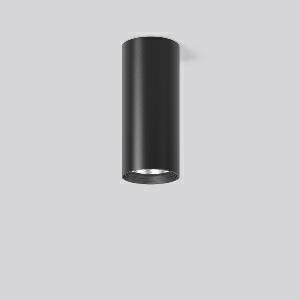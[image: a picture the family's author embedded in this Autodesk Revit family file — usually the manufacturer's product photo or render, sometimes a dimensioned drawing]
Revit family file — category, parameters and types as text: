
# Revit family: heledon_mini_a_931202_003_2_4c84
name_source: partatom
category: Lighting Fixtures
units: mm (PartAtom-declared; Revit-internal decimal feet)

## family parameters
Cut with Voids When Loaded = No
Host = Face
Light Source = No
Part Type = Normal
Room Calculation Point = No
Round Connector Dimension = Use Diameter
Shared = No

## types (1)
- HELEDON mini A (1 x LED Modul 927, 2400 lm, 2700)
    Apparent Load = 20 VA
    Approval mark = CE
    CIE Flux Codes = 95 99 100 100 100
    Color Rendering = 92
    Color Temperature = 2700
    Default Elevation = 1800 mm
    Description = Series: HELEDON mini
Cylindrical surface-mounted downlight. Housing: die-cast aluminium, powder-coated. Internal ceiling frame polycarbonate with bayonet mounting. Black plastic ring and recessed LED to prevent glare from the side. Optical assembly with reflector made of MIRO-Silver with 98% total light reflection for outstanding efficiency - can be changed without tools. Best colour rendering index Ra>90. Suitable for Ceiling mounting. Easy installation with a separate ceiling frame with bayonet mounting and plug connection. Driver integrated. Connected via plug-in connector. High quality converter without flickering and stroboscopic effect. The following accessories can be mounted without use of tools: interchangeable lenses, decorative glasses, honeycomb louvre, clear and frosted diffusers, white interchangeable plastic ring. 
Colour: deep black, matt (RAL 9005)
Diameter: 87 mm
Height: 197 mm
Lamp: LED
Socket: without socket
Colour temperature: 2700K
Colour rendering index (CRI): 92
System power: 20 W
Rated luminous flux: 2400 lm
Luminous efficiency: 120 lm/W
Control gear: Regulated power supply
Protection class: I
Type of protection: IP 20
    Height = 197 mm
    Lamp = 1 x LED Modul 927
    Lamp Light Flux = 2400 lm
    Lamp count = 1
    Length = 87 mm
    Lifetime = 50000 h
    Luminous efficacy = 120 lm/W
    Manufacturer = RZB
    ModVariant = No
    Model = 931202.003.2
    Mounting Place = Ceiling
    Mounting Type = Surface mounted
    Number of Poles = 1
    OnlyDefault = Yes
    Power Factor = 1
    Product Name = HELEDON mini A
    Product group = Surface mounted downlights
    ProductGroupID = 302
    Protection Class = Protection class I
    Protection Degree = IP 20
    RLX_Detail_Level = 1
    RLX_Emergency_Light_Flux = 0 lm
    RLX_Emergency_Type = 0
    RLX_Emergency_Type_DB = No
    RlxData = <blob elided: 107037 chars, md5=5782685c>
    Socket = socket
    Standby Power = 0 W
    System Light Flux = 2400 lm
    System Power = 20 W
    Type Comments = Product without accessories
    Type Image = 931188.003.jpg
    URL = http://relux.com
    VarID = ---
    Voltage = 230 V
    Voltage Range = 220-240 V
    Weight = 0.00 kg
    Width = 0 mm  [stored 0 ft]

note: [stored X ft] marks values corroborated as IEEE doubles in the binary element streams (Revit-internal decimal feet)

## geometry (parser evidence)
native form markers: Blend x4, Sweep x10
no freeform markers — native parametric forms only
